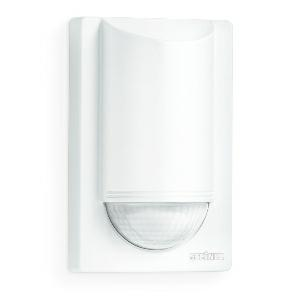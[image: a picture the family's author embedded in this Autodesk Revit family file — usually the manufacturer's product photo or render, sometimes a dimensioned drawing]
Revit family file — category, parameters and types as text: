
# Revit family: is_2180_eco_034696
name_source: partatom
category: Elektroinstallationen
revit_build: Autodesk Revit 2016 (Build: 20190508_0715(x64)
units: mm (PartAtom-declared; Revit-internal decimal feet)

## family parameters
Basisbauteil = Fläche
Beim Laden mit Abzugskörper schneiden = Nein
Bemaßung runder Anschluss = Durchmesser verwenden
Beschriftungsausrichtung beibehalten = Nein
Gemeinsam genutzt = Nein
Raumberechnungspunkt = Nein
Teiletyp = Normal

## types (1)
- IS 2180 ECO
    Apparent Load = 0 VA
    Beschreibung = Type: Motion detectors; Dimensions (L x W x H): 55 x 78 x 120 mm; Mains power supply: 230 – 240 V / 50 Hz; Sensor Technology: passive infrared; Application, place: Outdoors; Application, room: outdoors, front door, all round the building, terrace / balcony, courtyard & driveway; Installation site: wall, corner; Installation: Surface wiring; Switching zones: 504 switching zones; Electronic scalability: No; Mechanical scalability: No; Mounting height: 1,8 – 4 m; Optimum mounting height: 2 m; Detection angle: 180 °; Angle of aperture: 90 °; Sneak-by guard: Yes; Capability of masking out individual segments: Yes; Reach, radial: r = 2 m (6 m²) / r = 4 m (25 m²); Reach, tangential: r = 5 m (39 m²) / r = 12 m (226 m²); Twilight setting TEACH: No; Twilight setting: 2 – 2000 lx; Time setting: 5 sec – 15 min; Switching output 1, resistive: 2000 W; Switching output 1, number of LEDs / fluorescent lamps: 6 pcs.; Constant-lighting control: No; Basic light level function: No; Settings via: Potentiometers; With remote control: No; Interconnection: Yes; IP-rating: IP54; Material: Plastic; Ambient temperature: -20 – 50 °C; Colour: white; Colour, RAL: 9010; IDs, certificates: VDE; Manufacturer's Warranty: 5 years; Version: white; PU1, EAN: 4007841034696
    Height = 120 mm
    Hersteller = Steinel
    Length = 55 mm
    ModVariant = Nein
    Modell = 034696
    Mounting Type = Surface mounted
    Number of Poles = 1
    OnlyDefault = Ja
    Power Factor = 1
    Product Name = IS 2180 ECO
    Product group = Sensor-switched indoor light
    ProductGroupID = 30
    Protection Class = Protection class
    Protection Degree = IP 54
    RlxData = <blob elided: 31697 chars, md5=ad49f4bd>
    SensorDataFile = {"IESDataFiles":[]}
    Typenbild = produkt1_034696.jpg
    Typenkommentare = Product without accessories
    URL = http://relux.com
    VarID = ---
    Voltage = 0 V
    Vorgabe-Ansicht = 1800 mm
    Weight = 0.00 kg
    Width = 78 mm  [stored 0.255906 ft]

note: [stored X ft] marks values corroborated as IEEE doubles in the binary element streams (Revit-internal decimal feet)

## geometry (parser evidence)
native form markers: Sweep x10
no freeform markers — native parametric forms only
